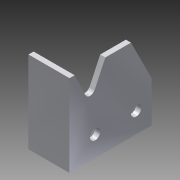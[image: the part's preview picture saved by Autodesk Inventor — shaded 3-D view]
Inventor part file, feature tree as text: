
AUTODESK INVENTOR PART (.ipt)
format: ipt  version: 2015 (Build 190159000, 159)  size: 144,384 bytes
history: native  units: in
note: dims shown in document units (in); Inventor stores cm internally (conversion verified against a paired STEP export)
features: sketch x5, extrude x4, projected_geometry x2, hole x1
ambient origin geometry x8: Origin, YZ Plane, XZ Plane, XY Plane, X Axis, Y Axis, Z Axis, Center Point
bodies: Solid1 (feature_tree)
feature tree (12):
  extrude  "Extrusion1"  Depth=0.125in
  extrude  "Extrusion2"  Depth=2.0in
  extrude  "Extrusion3"  Depth=1.0in
  extrude  "Extrusion4"  Depth=2.0in TaperAngle=0.0deg
  hole  "Hole1"  [1 undecoded]
  sketch  "Sketch1"  dims[d0=2.0in d1=0.125in]
  sketch  "Sketch2"  dims[d2=0.125in d3=2.0in]
  sketch  "Sketch3"  dims[d4=2.0in d5=0.0in d6=1.0in]
  projected_geometry  "Projected Loop1"
  projected_geometry  "Projected Loop2"
  sketch  "Sketch4"  dims[d7=2.0in d8=2.0in d9=0.0in]
  sketch  "Sketch5"  dims[d10=0.25in d11=0.75in d12=0.375in d13=0.5in d14=2.0in d15=0.0in d16=0.5in d17=1.0in d18=2.0in d19=0.0in d20=0.625in d21=0.5in d22=0.5in d23=0.375in d24=0.25in d25=0.75in d26=0.375in d27=0.25in d28=0.5635in d29=1.0in d30=0.8108in]
note: 1 required parameter value undecoded (feature->parameter linkage not recoverable at this tier; creation-order binding heuristic only, values carry confidence <= 0.55)
